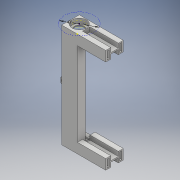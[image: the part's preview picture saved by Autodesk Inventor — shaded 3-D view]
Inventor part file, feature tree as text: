
AUTODESK INVENTOR PART (.ipt)
format: ipt  version: 2018 (Build 220112000, 112)  size: 327,680 bytes
history: native  units: mm
features: sketch x14, extrude x13, fillet x4
ambient origin geometry x8: Origin, YZ Plane, XZ Plane, XY Plane, X Axis, Y Axis, Z Axis, Center Point
bodies: Solid1 (feature_tree)
feature tree (31):
  extrude  "Extrusion1"  Depth=165.0mm
  extrude  "Extrusion2"  Depth=8.5mm
  extrude  "Extrusion3"  Depth=25.0mm TaperAngle=0.0deg
  extrude  "Extrusion4"  Depth=22.75mm
  extrude  "Extrusion5"  Depth=7.1mm
  extrude  "Extrusion6"  Depth=7.1mm TaperAngle=0.0deg
  fillet  "Fillet1"  Radius=5.0mm
  extrude  "Extrusion7"  Depth=10.0mm TaperAngle=0.0deg
  fillet  "Fillet2"  Radius=2.0mm
  extrude  "Extrusion8"  Depth=8.0mm
  extrude  "Extrusion9"  Depth=16.0mm
  fillet  "Fillet3"  Radius=8.0mm
  extrude  "Extrusion10"  Depth=6.0mm
  extrude  "Extrusion11"  Depth=3.5mm
  fillet  "Fillet4"  Radius=12.25mm
  sketch  "Sketch12"  dims[d33=3.5mm d34=12.25mm]
  extrude  "Extrusion12"  Depth=12.25mm
  extrude  "Extrusion13"  Depth=3.5mm
  sketch  "Sketch1"  dims[d0=25.0mm d1=165.0mm]
  sketch  "Sketch2"  dims[d2=3.0mm d3=0.0mm d4=8.5mm]
  sketch  "Sketch3"  dims[d5=8.5mm d6=25.0mm d7=0.0mm]
  sketch  "Sketch4"  dims[d8=25.0mm d9=22.75mm]
  sketch  "Sketch5"  dims[d10=7.1mm d11=0.0mm d12=15.5mm]
  sketch  "Sketch6"  dims[d13=165.0mm d14=0.0mm d15=7.1mm d16=0.0mm d17=5.0mm]
  sketch  "Sketch7"  dims[d18=5.0mm d19=10.0mm d20=0.0mm d21=2.0mm]
  sketch  "Sketch8"  dims[d22=16.0mm d23=8.0mm]
  sketch  "Sketch9"  dims[d24=16.0mm d25=16.0mm d26=8.0mm]
  sketch  "Sketch10"  dims[d27=45.0mm d28=0.0mm d29=6.0mm]
  sketch  "Sketch11"  dims[d30=12.25mm d31=3.5mm d32=12.25mm]
  sketch  "Sketch13"  dims[d35=12.25mm d36=3.5mm]
  sketch  "Sketch14"  dims[d37=40.0mm d38=0.0mm d39=1.0mm d40=2.0mm d41=8.0mm d42=1.0mm d43=2.0mm d44=12.0mm d45=0.0mm d46=6.0mm d47=6.0mm d48=4.0mm d49=8.0mm d50=6.5mm d51=0.0mm d52=6.35mm d53=8.0mm d54=0.0mm d55=6.5mm d56=47.0mm d57=1.0mm d58=7.0mm d59=0.0mm d60=7.1mm d61=0.0mm]
